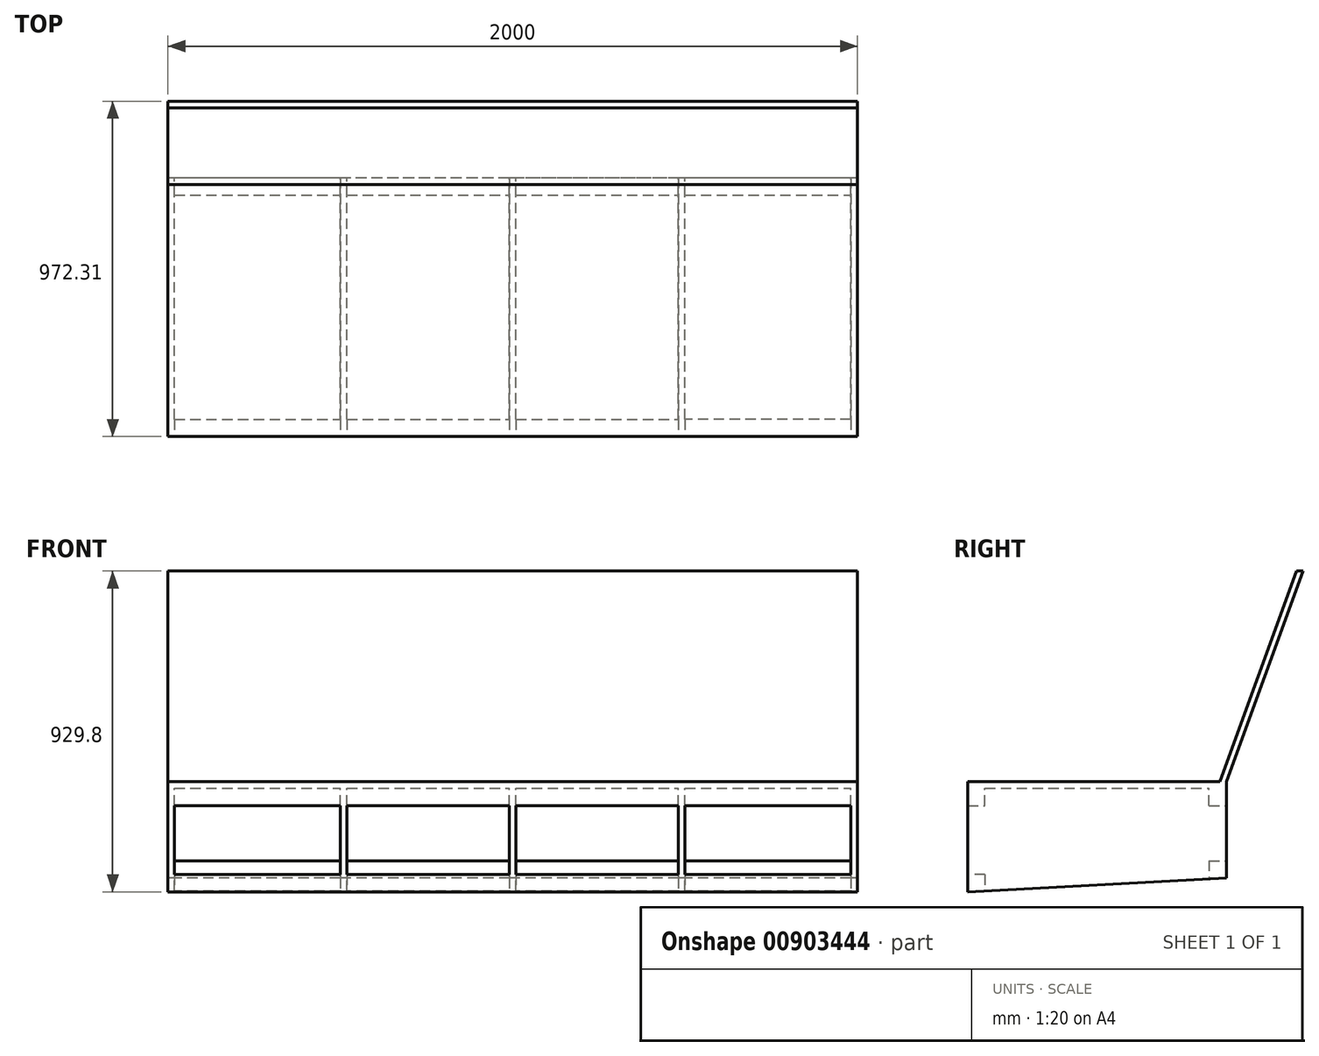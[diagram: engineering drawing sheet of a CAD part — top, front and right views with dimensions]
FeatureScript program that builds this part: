
annotation { "Feature Type Name" : "Feature", "Feature Type Description" : "" }
export const myFeature = defineFeature(function(context is Context, id is Id, definition is map)
    precondition{}
    {
        {
            var Q0;
            Q0=qCreatedBy(makeId("Top.planeOp"),FACE);
            var sketch = newSketch(context, id + "F0", { "sketchPlane" : qUnion([Q0])});
            skLineSegment(sketch, "E0.bottom", {"start": v(1000, 375) * mm, "end": v(-1000, 375) * mm});
            skLineSegment(sketch, "E0.top", {"start": v(1000, -375) * mm, "end": v(-1000, -375) * mm});
            skLineSegment(sketch, "E0.left", {"start": v(1000, 375) * mm, "end": v(1000, -375) * mm});
            skLineSegment(sketch, "E0.right", {"start": v(-1000, 375) * mm, "end": v(-1000, -375) * mm});
            skPoint(sketch, "E0.middle", {"position": v(0, 0) * mm});
            skSolve(sketch);
        }
        {
            var Q0;
            Q0=makeQuery(id+"F0.imprint","IMPRINT",FACE,{"disambiguationData":[TD([[makeQuery(id+"F0.imprint","IMPRINT",EDGE,{"derivedFrom":sQuery(id+"F0.wireOp",EDGE,"E0.bottom")}),1.0]])]});
            extrude(context, id + "F1", {"entities" : qUnion([Q0]), "depth" : 19 * mm, "offsetDistance" : 25 * mm});
        }
        {
            var Q0;
            Q0=makeQuery(id+"F1.opExtrude","CAP_FACE",FACE,{"disambiguationData":[OSD([sQuery(id+"F0.wireOp",EDGE,"E0.bottom"),sQuery(id+"F0.wireOp",EDGE,"E0.top"),sQuery(id+"F0.wireOp",EDGE,"E0.left"),sQuery(id+"F0.wireOp",EDGE,"E0.right")])],"isStart":true});
            var sketch = newSketch(context, id + "F2", { "sketchPlane" : qUnion([Q0])});
            skLineSegment(sketch, "E1.bottom", {"start": v(-1000, 375) * mm, "end": v(-981, 375) * mm});
            skLineSegment(sketch, "E1.top", {"start": v(-1000, -375) * mm, "end": v(-981, -375) * mm});
            skLineSegment(sketch, "E1.left", {"start": v(-1000, 375) * mm, "end": v(-1000, -375) * mm});
            skLineSegment(sketch, "E1.right", {"start": v(-981, 375) * mm, "end": v(-981, -375) * mm});
            skLineSegment(sketch, "E2.bottom", {"start": v(1000, 375) * mm, "end": v(981, 375) * mm});
            skLineSegment(sketch, "E2.top", {"start": v(1000, -375) * mm, "end": v(981, -375) * mm});
            skLineSegment(sketch, "E2.left", {"start": v(1000, 375) * mm, "end": v(1000, -375) * mm});
            skLineSegment(sketch, "E2.right", {"start": v(981, 375) * mm, "end": v(981, -375) * mm});
            skPoint(sketch, "E3", {"position": v(490.5, 0) * mm});
            skPoint(sketch, "E4", {"position": v(-490.5, 0) * mm});
            skLineSegment(sketch, "E5.bottom", {"start": v(-481, 375) * mm, "end": v(-500, 375) * mm});
            skLineSegment(sketch, "E5.top", {"start": v(-481, -375) * mm, "end": v(-500, -375) * mm});
            skLineSegment(sketch, "E5.left", {"start": v(-481, 375) * mm, "end": v(-481, -375) * mm});
            skLineSegment(sketch, "E5.right", {"start": v(-500, 375) * mm, "end": v(-500, -375) * mm});
            skLineSegment(sketch, "E6.bottom", {"start": v(500, 375) * mm, "end": v(481, 375) * mm});
            skLineSegment(sketch, "E6.top", {"start": v(500, -375) * mm, "end": v(481, -375) * mm});
            skLineSegment(sketch, "E6.left", {"start": v(500, 375) * mm, "end": v(500, -375) * mm});
            skLineSegment(sketch, "E6.right", {"start": v(481, 375) * mm, "end": v(481, -375) * mm});
            skLineSegment(sketch, "E7.bottom", {"start": v(9.5, 375) * mm, "end": v(-9.5, 375) * mm});
            skLineSegment(sketch, "E7.top", {"start": v(9.5, -375) * mm, "end": v(-9.5, -375) * mm});
            skLineSegment(sketch, "E7.left", {"start": v(9.5, 375) * mm, "end": v(9.5, -375) * mm});
            skLineSegment(sketch, "E7.right", {"start": v(-9.5, 375) * mm, "end": v(-9.5, -375) * mm});
            skPoint(sketch, "E7.middle", {"position": v(0, 0) * mm});
            skSolve(sketch);
        }
        {
            var Q0;
            Q0=makeQuery(id+"F2.imprint","IMPRINT",FACE,{"disambiguationData":[TD([[makeQuery(id+"F2.imprint","IMPRINT",EDGE,{"derivedFrom":sQuery(id+"F2.wireOp",EDGE,"E1.bottom")}),1.0]])]});
            var Q1;
            Q1=makeQuery(id+"F2.imprint","IMPRINT",FACE,{"disambiguationData":[TD([[makeQuery(id+"F2.imprint","IMPRINT",EDGE,{"derivedFrom":sQuery(id+"F2.wireOp",EDGE,"E5.bottom")}),1.0]])]});
            var Q2;
            Q2=makeQuery(id+"F2.imprint","IMPRINT",FACE,{"disambiguationData":[TD([[makeQuery(id+"F2.imprint","IMPRINT",EDGE,{"derivedFrom":sQuery(id+"F2.wireOp",EDGE,"E7.bottom")}),1.0]])]});
            var Q3;
            Q3=makeQuery(id+"F2.imprint","IMPRINT",FACE,{"disambiguationData":[TD([[makeQuery(id+"F2.imprint","IMPRINT",EDGE,{"derivedFrom":sQuery(id+"F2.wireOp",EDGE,"E6.bottom")}),1.0]])]});
            var Q4;
            Q4=makeQuery(id+"F2.imprint","IMPRINT",FACE,{"disambiguationData":[TD([[makeQuery(id+"F2.imprint","IMPRINT",EDGE,{"derivedFrom":sQuery(id+"F2.wireOp",EDGE,"E2.bottom")}),1.0]])]});
            extrude(context, id + "F3", {"entities" : qUnion([Q0, Q1, Q2, Q3, Q4]), "operationType" : NewBodyOperationType.ADD, "depth" : 300 * mm, "offsetDistance" : 25 * mm});
        }
        {
            var Q0;
            Q0=makeQuery(id+"F3.opExtrude","CAP_EDGE",EDGE,{"disambiguationData":[OSD([sQuery(id+"F2.wireOp",EDGE,"E2.top")])],"isStart":false});
            var Q1;
            Q1=makeQuery(id+"F3.opExtrude","CAP_EDGE",EDGE,{"disambiguationData":[OSD([sQuery(id+"F2.wireOp",EDGE,"E6.top")])],"isStart":false});
            var Q2;
            Q2=makeQuery(id+"F3.opExtrude","CAP_EDGE",EDGE,{"disambiguationData":[OSD([sQuery(id+"F2.wireOp",EDGE,"E7.top")])],"isStart":false});
            var Q3;
            Q3=makeQuery(id+"F3.opExtrude","CAP_EDGE",EDGE,{"disambiguationData":[OSD([sQuery(id+"F2.wireOp",EDGE,"E5.top")])],"isStart":false});
            var Q4;
            Q4=makeQuery(id+"F3.opExtrude","CAP_EDGE",EDGE,{"disambiguationData":[OSD([sQuery(id+"F2.wireOp",EDGE,"E1.top")])],"isStart":false});
            chamfer(context, id + "F4", {"entities" : qUnion([Q0, Q1, Q2, Q3, Q4]), "chamferType" : ChamferType.TWO_OFFSETS, "width1" : 750 * mm, "oppositeDirection" : true, "width2" : 40 * mm, "tangentPropagation" : true});
        }
        {
            var Q0;
            Q0=makeQuery(id+"F3.boolean.opBoolean","MERGE",FACE,{"derivedFrom":[makeQuery(id+"F1.opExtrude","SWEPT_FACE",FACE,{"disambiguationData":[OSD([sQuery(id+"F0.wireOp",EDGE,"E0.right")])]}),makeQuery(id+"F3.opExtrude","SWEPT_FACE",FACE,{"disambiguationData":[OSD([sQuery(id+"F2.wireOp",EDGE,"E1.left")])]})]});
            var sketch = newSketch(context, id + "F5", { "sketchPlane" : qUnion([Q0])});
            skLineSegment(sketch, "E8.bottom", {"start": v(-375, 19) * mm, "end": v(-356, 19) * mm});
            skLineSegment(sketch, "E8.top", {"start": v(-597.31, 629.8) * mm, "end": v(-578.31, 629.8) * mm});
            skLineSegment(sketch, "E8.right", {"start": v(-356, 19) * mm, "end": v(-578.31, 629.8) * mm});
            skLineSegment(sketch, "E9", {"start": v(-597.31, 629.8) * mm, "end": v(-375, 19) * mm});
            skSolve(sketch);
        }
        {
            var Q0;
            Q0=makeQuery(id+"F5.imprint","IMPRINT",FACE,{"disambiguationData":[TD([[makeQuery(id+"F5.imprint","IMPRINT",EDGE,{"derivedFrom":sQuery(id+"F5.wireOp",EDGE,"E8.bottom")}),1.0]])]});
            extrude(context, id + "F6", {"entities" : qUnion([Q0]), "operationType" : NewBodyOperationType.ADD, "oppositeDirection" : true, "depth" : 2000 * mm, "offsetDistance" : 25 * mm});
        }
        {
            var Q0;
            {var subQ0=sQuery(id+"F0.wireOp",EDGE,"E0.bottom");var subQ1=sQuery(id+"F0.wireOp",EDGE,"E0.top");Q0=makeQuery(id+"F3.boolean.opBoolean","SPLIT",FACE,{"disambiguationData":[TD([makeQuery(id+"F3.opExtrude","SWEPT_FACE",FACE,{"disambiguationData":[OSD([sQuery(id+"F2.wireOp",EDGE,"E2.right")])]})])],"derivedFrom":makeQuery(id+"F1.opExtrude","CAP_FACE",FACE,{"disambiguationData":[OSD([subQ0,subQ1,sQuery(id+"F0.wireOp",EDGE,"E0.left"),sQuery(id+"F0.wireOp",EDGE,"E0.right")])],"isStart":true})});}
            var sketch = newSketch(context, id + "F7", { "sketchPlane" : qUnion([Q0])});
            skLineSegment(sketch, "E10.bottom", {"start": v(981, 375) * mm, "end": v(500, 375) * mm});
            skLineSegment(sketch, "E10.top", {"start": v(981, 325) * mm, "end": v(500, 325) * mm});
            skLineSegment(sketch, "E10.left", {"start": v(981, 375) * mm, "end": v(981, 325) * mm});
            skLineSegment(sketch, "E10.right", {"start": v(500, 375) * mm, "end": v(500, 325) * mm});
            skLineSegment(sketch, "E11.bottom", {"start": v(500, -375) * mm, "end": v(981, -375) * mm});
            skLineSegment(sketch, "E11.top", {"start": v(500, -325) * mm, "end": v(981, -325) * mm});
            skLineSegment(sketch, "E11.left", {"start": v(500, -375) * mm, "end": v(500, -325) * mm});
            skLineSegment(sketch, "E11.right", {"start": v(981, -375) * mm, "end": v(981, -325) * mm});
            skSolve(sketch);
        }
        {
            var Q0;
            {var subQ0=sQuery(id+"F0.wireOp",EDGE,"E0.bottom");var subQ1=sQuery(id+"F0.wireOp",EDGE,"E0.top");Q0=makeQuery(id+"F3.boolean.opBoolean","SPLIT",FACE,{"disambiguationData":[TD([makeQuery(id+"F3.opExtrude","SWEPT_FACE",FACE,{"disambiguationData":[OSD([sQuery(id+"F2.wireOp",EDGE,"E6.right")])]})])],"derivedFrom":makeQuery(id+"F1.opExtrude","CAP_FACE",FACE,{"disambiguationData":[OSD([subQ0,subQ1,sQuery(id+"F0.wireOp",EDGE,"E0.left"),sQuery(id+"F0.wireOp",EDGE,"E0.right")])],"isStart":true})});}
            var sketch = newSketch(context, id + "F8", { "sketchPlane" : qUnion([Q0])});
            skLineSegment(sketch, "E12.bottom", {"start": v(9.5, 375) * mm, "end": v(481, 375) * mm});
            skLineSegment(sketch, "E12.top", {"start": v(9.5, 325) * mm, "end": v(481, 325) * mm});
            skLineSegment(sketch, "E12.left", {"start": v(9.5, 375) * mm, "end": v(9.5, 325) * mm});
            skLineSegment(sketch, "E12.right", {"start": v(481, 375) * mm, "end": v(481, 325) * mm});
            skLineSegment(sketch, "E13.bottom", {"start": v(9.5, -375) * mm, "end": v(481, -375) * mm});
            skLineSegment(sketch, "E13.top", {"start": v(9.5, -325) * mm, "end": v(481, -325) * mm});
            skLineSegment(sketch, "E13.left", {"start": v(9.5, -375) * mm, "end": v(9.5, -325) * mm});
            skLineSegment(sketch, "E13.right", {"start": v(481, -375) * mm, "end": v(481, -325) * mm});
            skSolve(sketch);
        }
        {
            var Q0;
            {var subQ0=sQuery(id+"F0.wireOp",EDGE,"E0.bottom");var subQ1=sQuery(id+"F0.wireOp",EDGE,"E0.top");Q0=makeQuery(id+"F3.boolean.opBoolean","SPLIT",FACE,{"disambiguationData":[TD([makeQuery(id+"F3.opExtrude","SWEPT_FACE",FACE,{"disambiguationData":[OSD([sQuery(id+"F2.wireOp",EDGE,"E5.left")])]})])],"derivedFrom":makeQuery(id+"F1.opExtrude","CAP_FACE",FACE,{"disambiguationData":[OSD([subQ0,subQ1,sQuery(id+"F0.wireOp",EDGE,"E0.left"),sQuery(id+"F0.wireOp",EDGE,"E0.right")])],"isStart":true})});}
            var sketch = newSketch(context, id + "F9", { "sketchPlane" : qUnion([Q0])});
            skLineSegment(sketch, "E14.bottom", {"start": v(-481, 375) * mm, "end": v(-9.5, 375) * mm});
            skLineSegment(sketch, "E14.top", {"start": v(-481, 325) * mm, "end": v(-9.5, 325) * mm});
            skLineSegment(sketch, "E14.left", {"start": v(-481, 375) * mm, "end": v(-481, 325) * mm});
            skLineSegment(sketch, "E14.right", {"start": v(-9.5, 375) * mm, "end": v(-9.5, 325) * mm});
            skLineSegment(sketch, "E15.bottom", {"start": v(-481, -375) * mm, "end": v(-9.5, -375) * mm});
            skLineSegment(sketch, "E15.top", {"start": v(-481, -325) * mm, "end": v(-9.5, -325) * mm});
            skLineSegment(sketch, "E15.left", {"start": v(-481, -375) * mm, "end": v(-481, -325) * mm});
            skLineSegment(sketch, "E15.right", {"start": v(-9.5, -375) * mm, "end": v(-9.5, -325) * mm});
            skSolve(sketch);
        }
        {
            var Q0;
            {var subQ0=sQuery(id+"F0.wireOp",EDGE,"E0.bottom");var subQ1=sQuery(id+"F0.wireOp",EDGE,"E0.top");Q0=makeQuery(id+"F3.boolean.opBoolean","SPLIT",FACE,{"disambiguationData":[TD([makeQuery(id+"F3.opExtrude","SWEPT_FACE",FACE,{"disambiguationData":[OSD([sQuery(id+"F2.wireOp",EDGE,"E1.right")])]})])],"derivedFrom":makeQuery(id+"F1.opExtrude","CAP_FACE",FACE,{"disambiguationData":[OSD([subQ0,subQ1,sQuery(id+"F0.wireOp",EDGE,"E0.left"),sQuery(id+"F0.wireOp",EDGE,"E0.right")])],"isStart":true})});}
            var sketch = newSketch(context, id + "F10", { "sketchPlane" : qUnion([Q0])});
            skLineSegment(sketch, "E16.bottom", {"start": v(-981, 375) * mm, "end": v(-500, 375) * mm});
            skLineSegment(sketch, "E16.top", {"start": v(-981, 325) * mm, "end": v(-500, 325) * mm});
            skLineSegment(sketch, "E16.left", {"start": v(-981, 375) * mm, "end": v(-981, 325) * mm});
            skLineSegment(sketch, "E16.right", {"start": v(-500, 375) * mm, "end": v(-500, 325) * mm});
            skLineSegment(sketch, "E17.bottom", {"start": v(-981, -375) * mm, "end": v(-500, -375) * mm});
            skLineSegment(sketch, "E17.top", {"start": v(-981, -325) * mm, "end": v(-500, -325) * mm});
            skLineSegment(sketch, "E17.left", {"start": v(-981, -375) * mm, "end": v(-981, -325) * mm});
            skLineSegment(sketch, "E17.right", {"start": v(-500, -375) * mm, "end": v(-500, -325) * mm});
            skSolve(sketch);
        }
        {
            var Q0;
            Q0=makeQuery(id+"F10.imprint","IMPRINT",FACE,{"disambiguationData":[TD([[makeQuery(id+"F10.imprint","IMPRINT",EDGE,{"derivedFrom":sQuery(id+"F10.wireOp",EDGE,"E16.bottom")}),1.0]])]});
            var Q1;
            Q1=makeQuery(id+"F10.imprint","IMPRINT",FACE,{"disambiguationData":[TD([[makeQuery(id+"F10.imprint","IMPRINT",EDGE,{"derivedFrom":sQuery(id+"F10.wireOp",EDGE,"E17.bottom")}),-1.0]])]});
            var Q2;
            Q2=makeQuery(id+"F9.imprint","IMPRINT",FACE,{"disambiguationData":[TD([[makeQuery(id+"F9.imprint","IMPRINT",EDGE,{"derivedFrom":sQuery(id+"F9.wireOp",EDGE,"E15.bottom")}),-1.0]])]});
            var Q3;
            Q3=makeQuery(id+"F9.imprint","IMPRINT",FACE,{"disambiguationData":[TD([[makeQuery(id+"F9.imprint","IMPRINT",EDGE,{"derivedFrom":sQuery(id+"F9.wireOp",EDGE,"E14.bottom")}),1.0]])]});
            var Q4;
            Q4=makeQuery(id+"F8.imprint","IMPRINT",FACE,{"disambiguationData":[TD([[makeQuery(id+"F8.imprint","IMPRINT",EDGE,{"derivedFrom":sQuery(id+"F8.wireOp",EDGE,"E12.bottom")}),1.0]])]});
            var Q5;
            Q5=makeQuery(id+"F7.imprint","IMPRINT",FACE,{"disambiguationData":[TD([[makeQuery(id+"F7.imprint","IMPRINT",EDGE,{"derivedFrom":sQuery(id+"F7.wireOp",EDGE,"E10.bottom")}),1.0]])]});
            var Q6;
            Q6=makeQuery(id+"F7.imprint","IMPRINT",FACE,{"disambiguationData":[TD([[makeQuery(id+"F7.imprint","IMPRINT",EDGE,{"derivedFrom":sQuery(id+"F7.wireOp",EDGE,"E11.bottom")}),-1.0]])]});
            var Q7;
            Q7=makeQuery(id+"F8.imprint","IMPRINT",FACE,{"disambiguationData":[TD([[makeQuery(id+"F8.imprint","IMPRINT",EDGE,{"derivedFrom":sQuery(id+"F8.wireOp",EDGE,"E13.bottom")}),-1.0]])]});
            extrude(context, id + "F11", {"entities" : qUnion([Q0, Q1, Q2, Q3, Q4, Q5, Q6, Q7]), "operationType" : NewBodyOperationType.ADD, "depth" : 50 * mm, "offsetDistance" : 25 * mm});
        }
        {
            var Q0;
            Q0=makeQuery(id+"F6.boolean.opBoolean","MERGE",FACE,{"derivedFrom":[makeQuery(id+"F3.boolean.opBoolean","MERGE",FACE,{"derivedFrom":[makeQuery(id+"F1.opExtrude","SWEPT_FACE",FACE,{"disambiguationData":[OSD([sQuery(id+"F0.wireOp",EDGE,"E0.right")])]}),makeQuery(id+"F3.opExtrude","SWEPT_FACE",FACE,{"disambiguationData":[OSD([sQuery(id+"F2.wireOp",EDGE,"E1.left")])]})]}),makeQuery(id+"F6.opExtrude","CAP_FACE",FACE,{"disambiguationData":[OSD([sQuery(id+"F5.wireOp",EDGE,"E8.bottom"),sQuery(id+"F5.wireOp",EDGE,"E8.top"),sQuery(id+"F5.wireOp",EDGE,"E8.right"),sQuery(id+"F5.wireOp",EDGE,"E9")])],"isStart":true})]});
            var sketch = newSketch(context, id + "F12", { "sketchPlane" : qUnion([Q0])});
            skLineSegment(sketch, "E18.bottom", {"start": v(-375, -260) * mm, "end": v(-325, -260) * mm});
            skLineSegment(sketch, "E18.top", {"start": v(-375, -210) * mm, "end": v(-325, -210) * mm});
            skLineSegment(sketch, "E18.left", {"start": v(-375, -260) * mm, "end": v(-375, -210) * mm});
            skLineSegment(sketch, "E18.right", {"start": v(-325, -260) * mm, "end": v(-325, -210) * mm});
            skLineSegment(sketch, "E19.bottom", {"start": v(375, -300) * mm, "end": v(325, -300) * mm});
            skLineSegment(sketch, "E19.top", {"start": v(375, -250) * mm, "end": v(325, -250) * mm});
            skLineSegment(sketch, "E19.left", {"start": v(375, -300) * mm, "end": v(375, -250) * mm});
            skLineSegment(sketch, "E19.right", {"start": v(325, -300) * mm, "end": v(325, -250) * mm});
            skSolve(sketch);
        }
        {
            var Q0;
            Q0=makeQuery(id+"F12.imprint","IMPRINT",FACE,{"disambiguationData":[TD([[makeQuery(id+"F12.imprint","IMPRINT",EDGE,{"derivedFrom":sQuery(id+"F12.wireOp",EDGE,"E18.bottom")}),1.0]])]});
            var Q1;
            {var subQ0=sQuery(id+"F12.wireOp",EDGE,"E19.top");Q1=makeQuery(id+"F12.imprint","IMPRINT",FACE,{"disambiguationData":[TD([[makeQuery(id+"F12.imprint","IMPRINT",EDGE,{"derivedFrom":subQ0}),1.0]])]});}
            extrude(context, id + "F13", {"entities" : qUnion([Q0, Q1]), "operationType" : NewBodyOperationType.ADD, "oppositeDirection" : true, "depth" : 2000 * mm, "offsetDistance" : 25 * mm});
        }
    });
